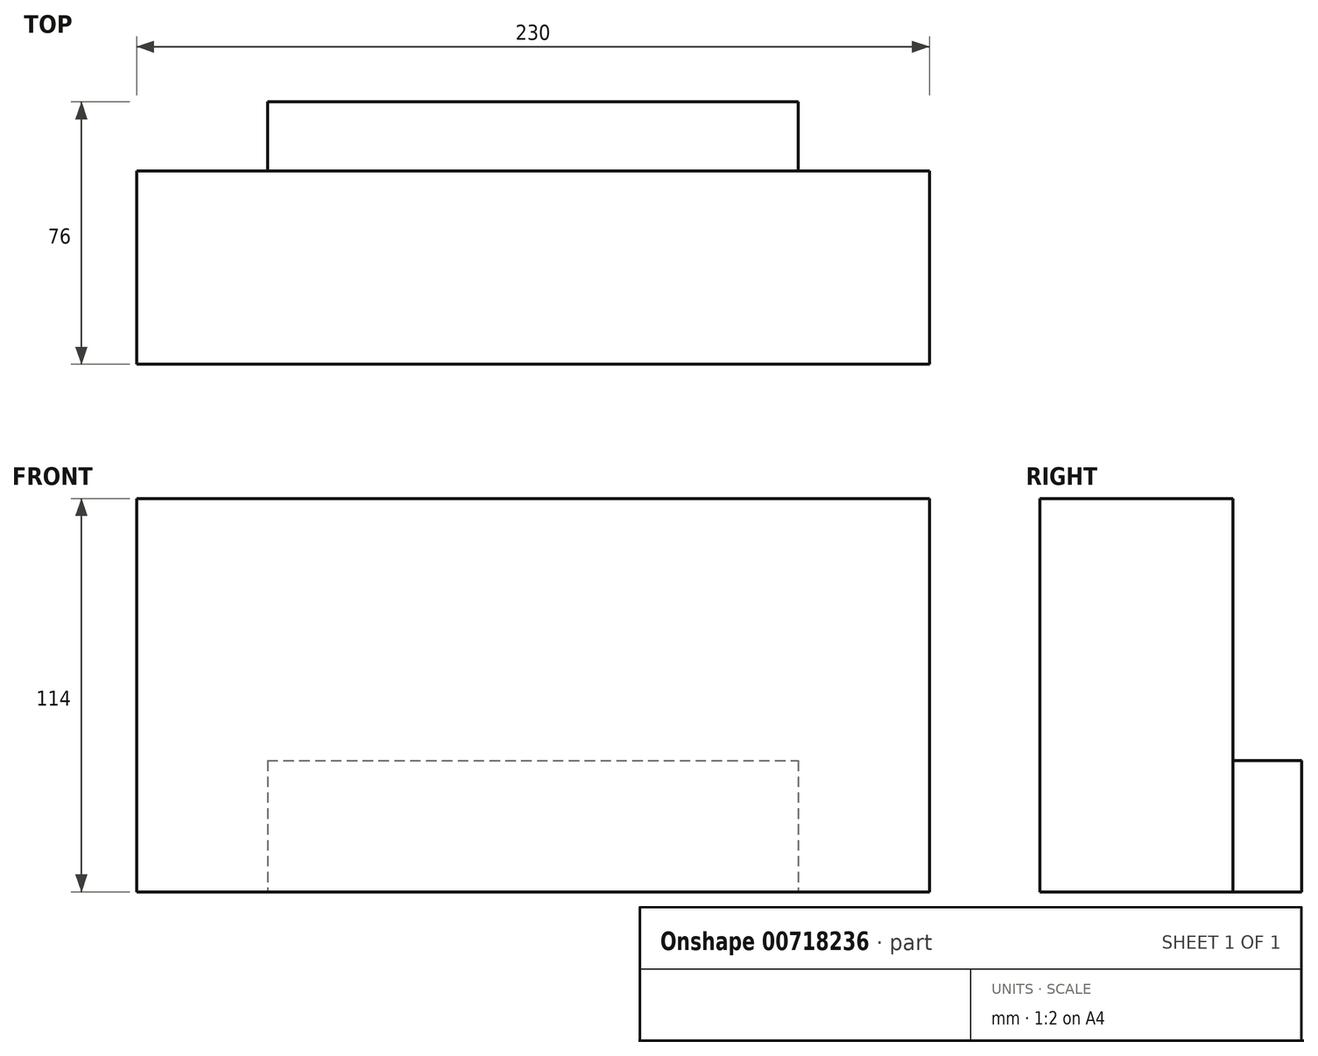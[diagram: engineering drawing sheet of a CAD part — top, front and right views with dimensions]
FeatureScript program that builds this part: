
annotation { "Feature Type Name" : "Feature", "Feature Type Description" : "" }
export const myFeature = defineFeature(function(context is Context, id is Id, definition is map)
    precondition{}
    {
        {
            var Q0;
            Q0=qCreatedBy(makeId("Front.planeOp"),FACE);
            var sketch = newSketch(context, id + "F0", { "sketchPlane" : qUnion([Q0])});
            skLineSegment(sketch, "E0.bottom", {"start": v(115, -57) * mm, "end": v(-115, -57) * mm});
            skLineSegment(sketch, "E0.top", {"start": v(115, 57) * mm, "end": v(-115, 57) * mm});
            skLineSegment(sketch, "E0.left", {"start": v(115, -57) * mm, "end": v(115, 57) * mm});
            skLineSegment(sketch, "E0.right", {"start": v(-115, -57) * mm, "end": v(-115, 57) * mm});
            skPoint(sketch, "E0.middle", {"position": v(0, 0) * mm});
            skSolve(sketch);
        }
        {
            var Q0;
            Q0=makeQuery(id+"F0.imprint","IMPRINT",FACE,{"disambiguationData":[TD([[makeQuery(id+"F0.imprint","IMPRINT",EDGE,{"derivedFrom":sQuery(id+"F0.wireOp",EDGE,"E0.bottom")}),-1.0]])]});
            extrude(context, id + "F1", {"entities" : qUnion([Q0]), "depth" : 76 * mm, "offsetDistance" : 25 * mm});
        }
        {
            var Q0;
            Q0=qCreatedBy(makeId("Right.planeOp"),FACE);
            cPlane(context, id + "F2", {"entities" : qUnion([Q0]), "cplaneType" : CPlaneType.OFFSET, "offset" : 115 * mm, "width" : 150 * mm, "height" : 150 * mm});
        }
        {
            var Q0;
            Q0=qCreatedBy(id+"F2.planeOp",FACE);
            var sketch = newSketch(context, id + "F3", { "sketchPlane" : qUnion([Q0])});
            skLineSegment(sketch, "E1.bottom", {"start": v(0, 57) * mm, "end": v(-20, 57) * mm});
            skLineSegment(sketch, "E1.top", {"start": v(0, -19) * mm, "end": v(-20, -19) * mm});
            skLineSegment(sketch, "E1.left", {"start": v(0, 57) * mm, "end": v(0, -19) * mm});
            skLineSegment(sketch, "E1.right", {"start": v(-20, 57) * mm, "end": v(-20, -19) * mm});
            skSolve(sketch);
        }
        {
            var Q0;
            Q0=makeQuery(id+"F3.imprint","IMPRINT",FACE,{"disambiguationData":[TD([[makeQuery(id+"F3.imprint","IMPRINT",EDGE,{"derivedFrom":sQuery(id+"F3.wireOp",EDGE,"E1.bottom")}),1.0]])]});
            extrude(context, id + "F4", {"entities" : qUnion([Q0]), "operationType" : NewBodyOperationType.REMOVE, "endBound" : BoundingType.THROUGH_ALL, "oppositeDirection" : true, "depth" : 25 * mm, "offsetDistance" : 25 * mm});
        }
        {
            var Q0;
            Q0=qCreatedBy(makeId("Top.planeOp"),FACE);
            cPlane(context, id + "F5", {"entities" : qUnion([Q0]), "cplaneType" : CPlaneType.OFFSET, "offset" : 57 * mm, "oppositeDirection" : true, "width" : 150 * mm, "height" : 150 * mm});
        }
        {
            var Q0;
            Q0=qCreatedBy(id+"F5.planeOp",FACE);
            var sketch = newSketch(context, id + "F6", { "sketchPlane" : qUnion([Q0])});
            skLineSegment(sketch, "E2.bottom", {"start": v(-115, -20) * mm, "end": v(-77, -20) * mm});
            skLineSegment(sketch, "E2.top", {"start": v(-115, 0) * mm, "end": v(-77, 0) * mm});
            skLineSegment(sketch, "E2.left", {"start": v(-115, -20) * mm, "end": v(-115, 0) * mm});
            skLineSegment(sketch, "E2.right", {"start": v(-77, -20) * mm, "end": v(-77, 0) * mm});
            skLineSegment(sketch, "E3.bottom", {"start": v(115, -20) * mm, "end": v(77, -20) * mm});
            skLineSegment(sketch, "E3.top", {"start": v(115, 0) * mm, "end": v(77, 0) * mm});
            skLineSegment(sketch, "E3.left", {"start": v(115, -20) * mm, "end": v(115, 0) * mm});
            skLineSegment(sketch, "E3.right", {"start": v(77, -20) * mm, "end": v(77, 0) * mm});
            skSolve(sketch);
        }
        {
            var Q0;
            Q0=makeQuery(id+"F6.imprint","IMPRINT",FACE,{"disambiguationData":[TD([[makeQuery(id+"F6.imprint","IMPRINT",EDGE,{"derivedFrom":sQuery(id+"F6.wireOp",EDGE,"E2.bottom")}),1.0]])]});
            var Q1;
            Q1=makeQuery(id+"F6.imprint","IMPRINT",FACE,{"disambiguationData":[TD([[makeQuery(id+"F6.imprint","IMPRINT",EDGE,{"derivedFrom":sQuery(id+"F6.wireOp",EDGE,"E3.bottom")}),-1.0]])]});
            extrude(context, id + "F7", {"entities" : qUnion([Q0, Q1]), "operationType" : NewBodyOperationType.REMOVE, "endBound" : BoundingType.THROUGH_ALL, "depth" : 25 * mm, "offsetDistance" : 25 * mm});
        }
    });
